# Revit family: 321321321
name_source: partatom
category: Furniture
revit_build: Autodesk Revit 2016 (Build: 20150220_1215(x64)
units: mm (PartAtom-declared; Revit-internal decimal feet)

## family parameters
Always vertical = Yes
Cut with Voids When Loaded = No
OmniClass Number = 23.40.20.00
OmniClass Title = General Furniture and Specialties
Room Calculation Point = No
Shared = No
Work Plane-Based = No

## types (16) — shared parameters
Arm Pad = okm_G721
Assembly Code = E2020200
Body = okm_G721
Casters = okm_G155
D = 600 mm
Frame = okm_Silver FX4
H = 1080 mm  [stored 3.54331 ft]
Keynote = 12490
Kind = Chair
Leg = okm_Silver FX4
Manufacturer = Okamura Corporation
Other = okm_G155
Product Categories = Office seating
URL = http://www.okamura.co.jp
W = 676 mm

## per-type parameters (varying)
| type | Back Mesh | Product Code/Color | Seat Cushion |
| FPC2(White) | okm_FSP2 | CC83BS_FPC2 | okm_FEA3 |
| FPC7(Beige) | okm_FSP7 | CC83BS_FPC7 | okm_FEA2 |
| FPC8(Dark Brown) | okm_FSP8 | CC83BS_FPC8 | okm_FGE8 |
| FPC3(Light Gray) | okm_FSR3 | CC83BS_FPC3 | okm_FBA3 |
| FPD2(Medium Gray) | okm_FSR2 | CC83BS_FPD2 | okm_FPE2 |
| FPC1(Black) | okm_FSP1 | CC83BS_FPC1 | okm_FBA1 |
| FPC4(Dark Blue) | okm_FSR4 | CC83BS_FPC4 | okm_FBA4 |
| FPC6(Sage) | okm_FTY6 | CC83BS_FPC6 | okm_FPE6 |
| FPD5(Dark Green) | okm_FSR5 | CC83BS_FPD5 | okm_FPE5 |
| FPC5(Green) | okm_FTY5 | CC83BS_FPC5 | okm_FPF5 |
| FPD9(Yellow) | okm_FSR9 | CC83BS_FPD9 | okm_FPB9 |
| FPD8(Orange Red) | okm_FTY8 | CC83BS_FPD8 | okm_FPE8 |
| FPC9(Red) | okm_FSP9 | CC83BS_FPC9 | okm_FPE9 |
| FPT2(White) | okm_FSP2 | CC83BS_FPT2 | okm_PC18 |
| FPT7(Beige) | okm_FSP7 | CC83BS_FPT7 | okm_PD35 |
| FPT1(Black) | okm_FSP1 | CC83BS_FPT1 | okm_P676 |

note: [stored X ft] marks values corroborated as IEEE doubles in the binary element streams (Revit-internal decimal feet)

## geometry (parser evidence)
native form markers: Sweep x2
no freeform markers — native parametric forms only
